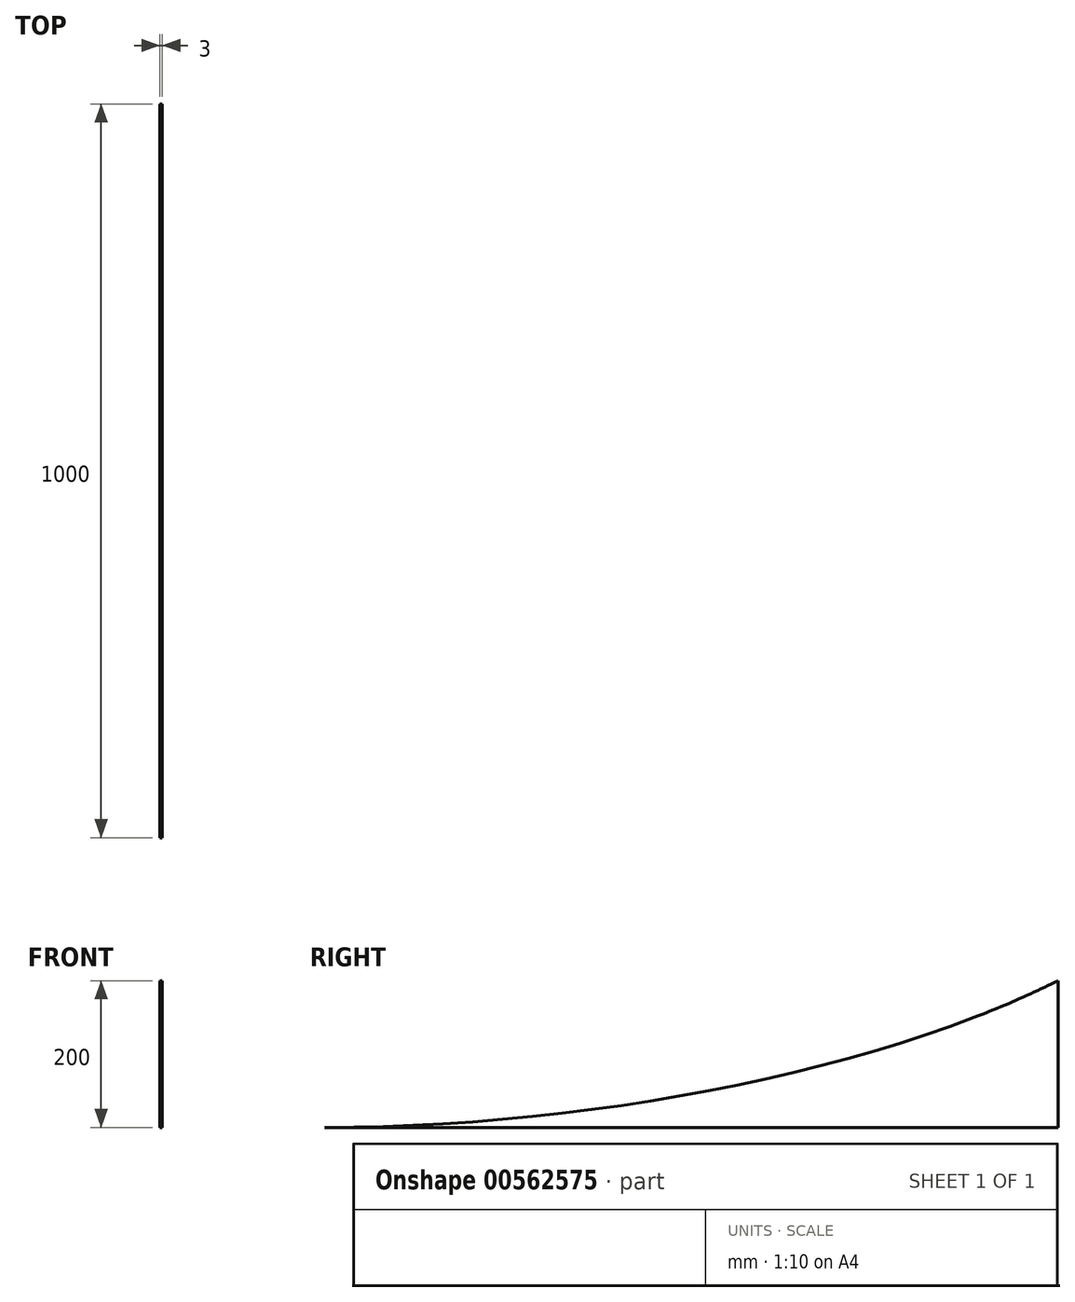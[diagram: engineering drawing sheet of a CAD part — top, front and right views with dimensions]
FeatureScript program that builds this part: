
annotation { "Feature Type Name" : "Feature", "Feature Type Description" : "" }
export const myFeature = defineFeature(function(context is Context, id is Id, definition is map)
    precondition{}
    {
        {
            var Q0;
            Q0=qCreatedBy(makeId("Right.planeOp"),FACE);
            var sketch = newSketch(context, id + "F0", { "sketchPlane" : qUnion([Q0])});
            skLineSegment(sketch, "E0", {"start": v(-467.1, -51.46) * mm, "end": v(532.9, -51.46) * mm});
            skLineSegment(sketch, "E1", {"start": v(532.9, -51.46) * mm, "end": v(532.9, 148.54) * mm});
            skFitSpline(sketch, "E2", {"points": [v(-467.1, -51.46) * mm, v(532.9, 148.54) * mm], "startDerivative": vector(1064.65, 0) * mm, "endDerivative": vector(757.35, 377.28) * mm});
            skLineSegment(sketch, "E3", {"start": v(418.41, -51.46) * mm, "end": v(418.41, 98.54) * mm});
            skLineSegment(sketch, "E4", {"start": v(418.41, -51.46) * mm, "end": v(393.41, -51.46) * mm});
            skSolve(sketch);
        }
        {
            var Q0;
            Q0 = qSketchRegion(id + "F0", true);
            extrude(context, id + "F1", {"entities" : qUnion([Q0]), "endBound" : BoundingType.SYMMETRIC, "depth" : 3 * mm, "offsetDistance" : 25 * mm});
        }
    });
